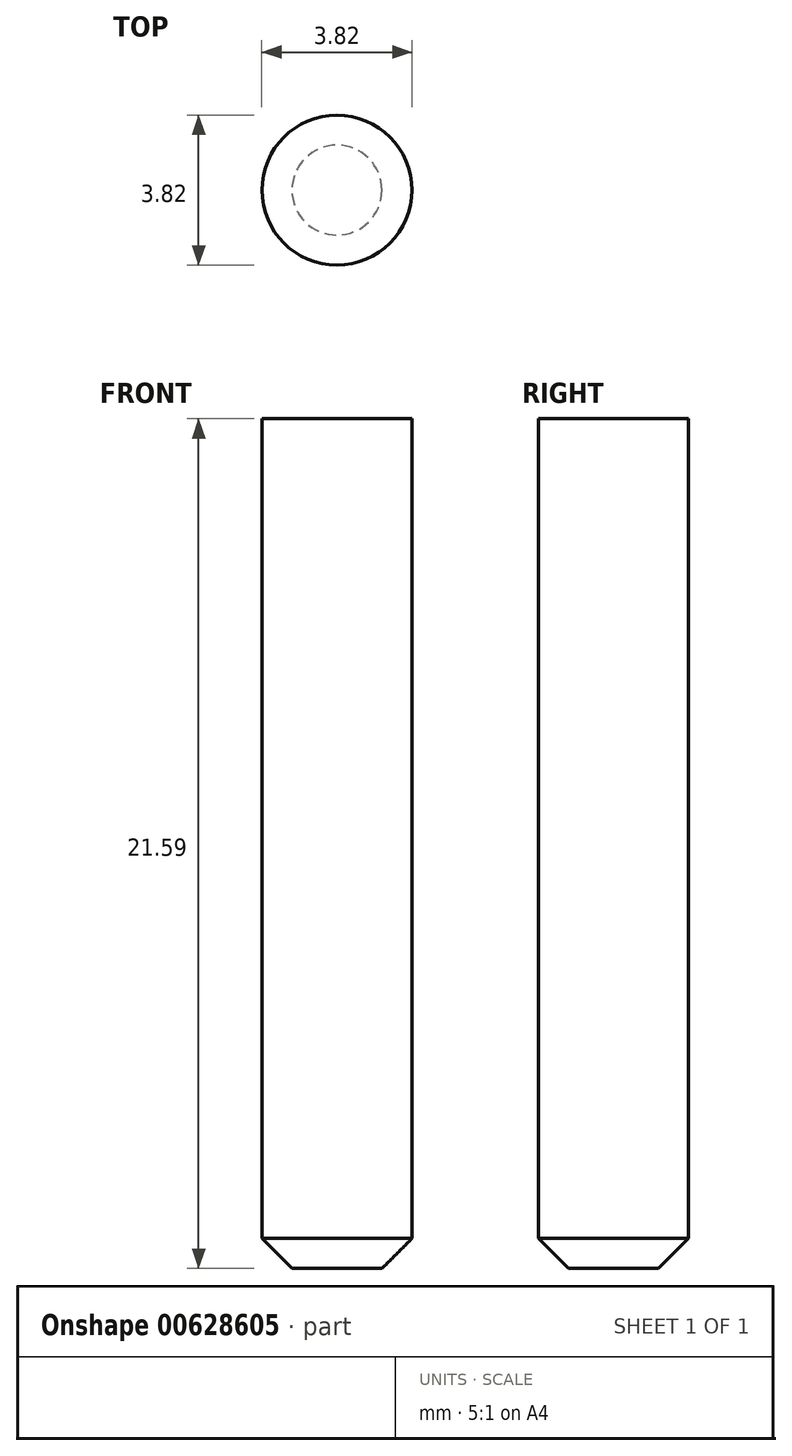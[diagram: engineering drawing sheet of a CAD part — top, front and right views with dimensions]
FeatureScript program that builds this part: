
annotation { "Feature Type Name" : "Feature", "Feature Type Description" : "" }
export const myFeature = defineFeature(function(context is Context, id is Id, definition is map)
    precondition{}
    {
        {
            var Q0;
            Q0=qCreatedBy(makeId("Top.planeOp"),FACE);
            var sketch = newSketch(context, id + "F0", { "sketchPlane" : qUnion([Q0])});
            skCircle(sketch, "E0", {"center": v(0, 0) * mm, "radius": 1.9 * mm});
            skSolve(sketch);
        }
        {
            var Q0;
            Q0=makeQuery(id+"F0.imprint","IMPRINT",FACE,{"disambiguationData":[TD([[makeQuery(id+"F0.imprint","IMPRINT",EDGE,{"derivedFrom":sQuery(id+"F0.wireOp",EDGE,"E0")}),1.0]])]});
            extrude(context, id + "F1", {"entities" : qUnion([Q0]), "depth" : 25.4 * mm, "offsetDistance" : 25.4 * mm});
        }
        {
            var Q0;
            Q0=makeQuery(id+"F1.opExtrude","CAP_EDGE",EDGE,{"disambiguationData":[OSD([sQuery(id+"F0.wireOp",EDGE,"E0")])],"isStart":true});
            chamfer(context, id + "F2", {"entities" : qUnion([Q0]), "width" : 0.76 * mm, "tangentPropagation" : true});
        }
        {
            var Q0;
            Q0=makeQuery(id+"F1.opExtrude","CAP_FACE",FACE,{"disambiguationData":[OSD([sQuery(id+"F0.wireOp",EDGE,"E0")])],"isStart":false});
            extrude(context, id + "F3", {"entities" : qUnion([Q0]), "operationType" : NewBodyOperationType.REMOVE, "oppositeDirection" : true, "depth" : 7.62 * mm, "offsetDistance" : 25.4 * mm});
        }
        {
            var Q0;
            Q0=makeQuery(id+"F3.boolean.opBoolean","COPY",FACE,{"derivedFrom":makeQuery(id+"F3.opExtrude","CAP_FACE",FACE,{"disambiguationData":[OSD([sQuery(id+"F0.wireOp",EDGE,"E0")])],"isStart":false})});
            extrude(context, id + "F4", {"entities" : qUnion([Q0]), "operationType" : NewBodyOperationType.ADD, "depth" : 3.8 * mm, "offsetDistance" : 25.4 * mm});
        }
    });
